# Revit family: F186 Cobble Ottoman
name_source: partatom
category: Furniture Systems
units: mm (PartAtom-declared; Revit-internal decimal feet)

## family parameters
Always vertical = Yes
Cut with Voids When Loaded = No
Enable Cutting in Views = No
Part Type = Normal
Room Calculation Point = No
Round Connector Dimension = Use Diameter
Shared = No
Work Plane-Based = No

## types (6) — shared parameters
3" Rectangle Leg = <By Category>
Base H = 2 "
Fabric = <By Category>
Glide = <By Category>
Low Profile = Black
Manufacturer = FOMCORE
URL = https://fomcore.com
zero-valued in all types: Default Elevation

## per-type parameters (varying)
| type | Base | Base Ins | Center H | Description | G1 | L1 | Model |
| 16"H - Cobble Ottoman - G1 | No | Yes | 13 " | 28" Cobble, 24"Dx16"H, 1"Glide | Yes | No | F186-28X24X16-G1 |
| 10"H - Cobble Ottoman - G1 | No | Yes | 7 " | 28" Cobble, 24"Dx10"H, 1"Glide | Yes | No | F186-28X24X10-G1 |
| 16"H - Cobble Ottoman - L1 | No | Yes | 13 " | 28" Cobble, 24"Dx16"H, 1" Low Profile Black Leg | No | Yes | F186-28X24X16-L1 |
| 16"H - Cobble Ottoman - Z | Yes | No | 12 " | 28" Cobble, 24"Dx16"H, Zippered | No | No | F186-28X24X16-Z |
| 10"H - Cobble Ottoman - L1 | No | Yes | 7 " | 28" Cobble, 24"Dx10"H, 1" Low Profile Black Leg | No | Yes | F186-28X24X10-L1 |
| 10"H - Cobble Ottoman - Z | Yes | No | 6 " | 28" Cobble, 24"Dx10"H, Zippered | No | No | F186-28X24X10-Z |

## geometry (parser evidence)
native form markers: Sweep x16
no freeform markers — native parametric forms only
